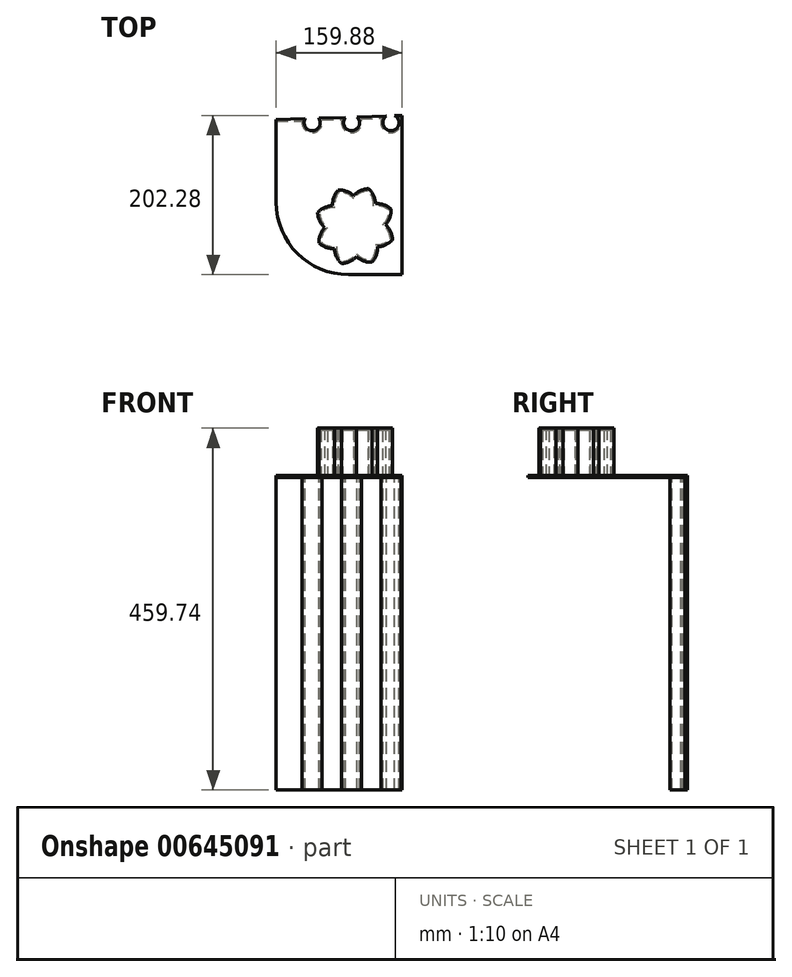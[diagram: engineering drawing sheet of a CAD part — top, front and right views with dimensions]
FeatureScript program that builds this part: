
annotation { "Feature Type Name" : "Feature", "Feature Type Description" : "" }
export const myFeature = defineFeature(function(context is Context, id is Id, definition is map)
    precondition{}
    {
        {
            var Q0;
            Q0=qCreatedBy(makeId("Top.planeOp"),FACE);
            var sketch = newSketch(context, id + "F0", { "sketchPlane" : qUnion([Q0])});
            skLineSegment(sketch, "E0", {"start": v(0, -62.86) * mm, "end": v(-45.7, -62.86) * mm});
            skLineSegment(sketch, "E1", {"start": v(-45.7, 35.56) * mm, "end": v(-45.7, 35.56) * mm});
            skLineSegment(sketch, "E2", {"start": v(-45.7, 35.56) * mm, "end": v(-45.7, -62.86) * mm});
            skLineSegment(sketch, "E3.MirrorCS", {"start": v(-45.7, 35.56) * mm, "end": v(-45.7, 133.98) * mm});
            skLineSegment(sketch, "E4", {"start": v(0, -62.86) * mm, "end": v(57.09, -62.86) * mm});
            skLineSegment(sketch, "E5.MirrorCS", {"start": v(114.18, -62.86) * mm, "end": v(57.09, -62.86) * mm});
            skLineSegment(sketch, "E6.MirrorCS", {"start": v(114.18, 35.56) * mm, "end": v(114.18, 133.98) * mm});
            skLineSegment(sketch, "E7.MirrorCS", {"start": v(114.18, 35.56) * mm, "end": v(114.18, -62.86) * mm});
            skLineSegment(sketch, "E8", {"start": v(-45.7, 133.98) * mm, "end": v(114.18, 139.42) * mm});
            skLineSegment(sketch, "E9", {"start": v(114.18, 139.42) * mm, "end": v(114.18, 126.98) * mm});
            skPoint(sketch, "E10.0", {"position": v(0, 0) * mm});
            skSolve(sketch);
        }
        {
            var Q0;
            Q0 = qSketchRegion(id + "F0", true);
            extrude(context, id + "F1", {"entities" : qUnion([Q0]), "oppositeDirection" : true, "depth" : 228.85 * mm, "offsetDistance" : 25.4 * mm, "hasSecondDirection" : true, "secondDirectionOppositeDirection" : false, "secondDirectionDepth" : 170.7 * mm});
        }
        {
            var Q0;
            Q0=makeQuery(id+"F1.opExtrude","CAP_FACE",FACE,{"disambiguationData":[OSD([sQuery(id+"F0.wireOp",EDGE,"E0"),sQuery(id+"F0.wireOp",EDGE,"E3.MirrorCS"),sQuery(id+"F0.wireOp",EDGE,"E2"),sQuery(id+"F0.wireOp",EDGE,"E4"),sQuery(id+"F0.wireOp",EDGE,"E5.MirrorCS"),sQuery(id+"F0.wireOp",EDGE,"E6.MirrorCS"),sQuery(id+"F0.wireOp",EDGE,"E7.MirrorCS"),sQuery(id+"F0.wireOp",EDGE,"E8"),sQuery(id+"F0.wireOp",EDGE,"E9")])],"isStart":true});
            var sketch = newSketch(context, id + "F2", { "sketchPlane" : qUnion([Q0])});
            skCircle(sketch, "E11", {"center": v(0, 130.15) * mm, "radius": 10.85 * mm});
            skArc(sketch, "E12", {"start": v(33.03, 44.58) * mm, "mid": v(27.5, 35.43) * mm, "end": v(25.9, 24.87) * mm});
            skCircle(sketch, "E13.1.0.0", {"center": v(50.04, 130.15) * mm, "radius": 10.85 * mm});
            skCircle(sketch, "E13.2.0.0", {"center": v(100.08, 130.15) * mm, "radius": 10.85 * mm});
            skLineSegment(sketch, "E13.direction1", {"start": v(0, 130.15) * mm, "end": v(50.04, 130.15) * mm, "construction": true});
            skArc(sketch, "E14.1.0", {"start": v(6.93, 15.97) * mm, "mid": v(9.49, 5.6) * mm, "end": v(15.83, -3) * mm});
            skArc(sketch, "E14.2.0", {"start": v(8.7, -22.72) * mm, "mid": v(17.85, -28.24) * mm, "end": v(28.42, -29.84) * mm});
            skArc(sketch, "E14.3.0", {"start": v(37.32, -48.82) * mm, "mid": v(47.69, -46.25) * mm, "end": v(56.3, -39.92) * mm});
            skArc(sketch, "E14.4.0", {"start": v(76, -47.04) * mm, "mid": v(81.53, -37.9) * mm, "end": v(83.13, -27.33) * mm});
            skArc(sketch, "E14.5.0", {"start": v(102.1, -18.43) * mm, "mid": v(99.54, -8.05) * mm, "end": v(93.2, 0.55) * mm});
            skArc(sketch, "E14.6.0", {"start": v(100.33, 20.26) * mm, "mid": v(91.18, 25.78) * mm, "end": v(80.61, 27.38) * mm});
            skArc(sketch, "E14.7.0", {"start": v(71.71, 46.36) * mm, "mid": v(61.34, 43.8) * mm, "end": v(52.74, 37.46) * mm});
            skPoint(sketch, "E14.center", {"position": v(54.51, -1.23) * mm});
            skArc(sketch, "E15.trimOffspring", {"start": v(15.83, -3) * mm, "mid": v(10.3, -12.15) * mm, "end": v(8.7, -22.72) * mm});
            skArc(sketch, "E16.trimOffspring", {"start": v(25.9, 24.87) * mm, "mid": v(15.53, 22.3) * mm, "end": v(6.93, 15.97) * mm});
            skArc(sketch, "E17.trimOffspring", {"start": v(52.74, 37.46) * mm, "mid": v(43.59, 42.98) * mm, "end": v(33.03, 44.58) * mm});
            skArc(sketch, "E18.trimOffspring", {"start": v(83.13, -27.33) * mm, "mid": v(93.5, -24.77) * mm, "end": v(102.1, -18.43) * mm});
            skArc(sketch, "E19.trimOffspring", {"start": v(56.3, -39.92) * mm, "mid": v(65.44, -45.44) * mm, "end": v(76, -47.04) * mm});
            skArc(sketch, "E20.trimOffspring", {"start": v(80.61, 27.38) * mm, "mid": v(78.05, 37.76) * mm, "end": v(71.71, 46.36) * mm});
            skArc(sketch, "E21.trimOffspring", {"start": v(93.2, 0.55) * mm, "mid": v(98.72, 9.7) * mm, "end": v(100.33, 20.26) * mm});
            skArc(sketch, "E22.trimOffspring", {"start": v(28.42, -29.84) * mm, "mid": v(30.98, -40.22) * mm, "end": v(37.32, -48.82) * mm});
            skSolve(sketch);
        }
        {
            var Q0;
            Q0=sQuery(id+"F2.wireOp",VERTEX,"E13.direction1.start");
            var Q1;
            Q1=sQuery(id+"F2.wireOp",VERTEX,"E13.direction1.end");
            var Q2;
            Q2=sQuery(id+"F2.wireOp",VERTEX,"E13.2.0.0.center");
            var Q3;
            Q3=makeQuery(id+"F1.opExtrude","SWEPT_BODY",BODY,{"disambiguationData":[OSD([sQuery(id+"F0.wireOp",EDGE,"E0"),sQuery(id+"F0.wireOp",EDGE,"E3.MirrorCS"),sQuery(id+"F0.wireOp",EDGE,"E2"),sQuery(id+"F0.wireOp",EDGE,"E4"),sQuery(id+"F0.wireOp",EDGE,"E5.MirrorCS"),sQuery(id+"F0.wireOp",EDGE,"E6.MirrorCS"),sQuery(id+"F0.wireOp",EDGE,"E7.MirrorCS"),sQuery(id+"F0.wireOp",EDGE,"E8"),sQuery(id+"F0.wireOp",EDGE,"E9")])]});
            hole(context, id + "F3", {"style" : HoleStyle.SIMPLE, "endStyle" : HoleEndStyle.THROUGH, "holeDiameter" : 20.32 * mm, "majorDiameter" : 6.35 * mm, "isTappedThrough" : true, "tappedDepth" : 12.7 * mm, "tapClearance" : 3, "locations" : qUnion([Q0, Q1, Q2]), "scope" : qUnion([Q3])});
        }
        {
            var Q0;
            Q0=makeQuery(id+"F1.opExtrude","SWEPT_EDGE",EDGE,{"disambiguationData":[OSD([sQuery(id+"F0.wireOp",EDGE,"E0"),sQuery(id+"F0.wireOp",EDGE,"E2")])]});
            fillet(context, id + "F4", {"entities" : qUnion([Q0]), "radius" : 91.98 * mm, "tangentPropagation" : true, "allowEdgeOverflow" : false});
        }
        {
            var Q0;
            Q0=makeQuery(id+"F2.imprint","IMPRINT",FACE,{"disambiguationData":[TD([[makeQuery(id+"F2.imprint","IMPRINT",EDGE,{"derivedFrom":sQuery(id+"F2.wireOp",EDGE,"E12")}),1.0]])]});
            extrude(context, id + "F5", {"entities" : qUnion([Q0]), "operationType" : NewBodyOperationType.ADD, "depth" : 60.2 * mm, "offsetDistance" : 25.4 * mm});
        }
        {
            var Q0;
            Q0=makeQuery(id+"F4.opFillet","BLEND_FACE",FACE,{"disambiguationData":[OSD([sQuery(id+"F0.wireOp",EDGE,"E0"),sQuery(id+"F0.wireOp",EDGE,"E2")])]});
            var Q1;
            Q1=makeQuery(id+"F1.opExtrude","SWEPT_FACE",FACE,{"disambiguationData":[OSD([sQuery(id+"F0.wireOp",EDGE,"E3.MirrorCS"),sQuery(id+"F0.wireOp",EDGE,"E2")])]});
            var Q2;
            Q2=makeQuery(id+"F1.opExtrude","CAP_FACE",FACE,{"disambiguationData":[OSD([sQuery(id+"F0.wireOp",EDGE,"E0"),sQuery(id+"F0.wireOp",EDGE,"E3.MirrorCS"),sQuery(id+"F0.wireOp",EDGE,"E2"),sQuery(id+"F0.wireOp",EDGE,"E4"),sQuery(id+"F0.wireOp",EDGE,"E5.MirrorCS"),sQuery(id+"F0.wireOp",EDGE,"E6.MirrorCS"),sQuery(id+"F0.wireOp",EDGE,"E7.MirrorCS"),sQuery(id+"F0.wireOp",EDGE,"E8"),sQuery(id+"F0.wireOp",EDGE,"E9")])],"isStart":false});
            var Q3;
            Q3=makeQuery(id+"F1.opExtrude","SWEPT_FACE",FACE,{"disambiguationData":[OSD([sQuery(id+"F0.wireOp",EDGE,"E6.MirrorCS"),sQuery(id+"F0.wireOp",EDGE,"E7.MirrorCS"),sQuery(id+"F0.wireOp",EDGE,"E9")])]});
            var Q4;
            Q4=makeQuery(id+"F1.opExtrude","SWEPT_FACE",FACE,{"disambiguationData":[OSD([sQuery(id+"F0.wireOp",EDGE,"E0"),sQuery(id+"F0.wireOp",EDGE,"E4"),sQuery(id+"F0.wireOp",EDGE,"E5.MirrorCS")])]});
            shell(context, id + "F6", {"entities" : qUnion([Q0, Q1, Q2, Q3, Q4]), "thickness" : 2.54 * mm});
        }
    });
